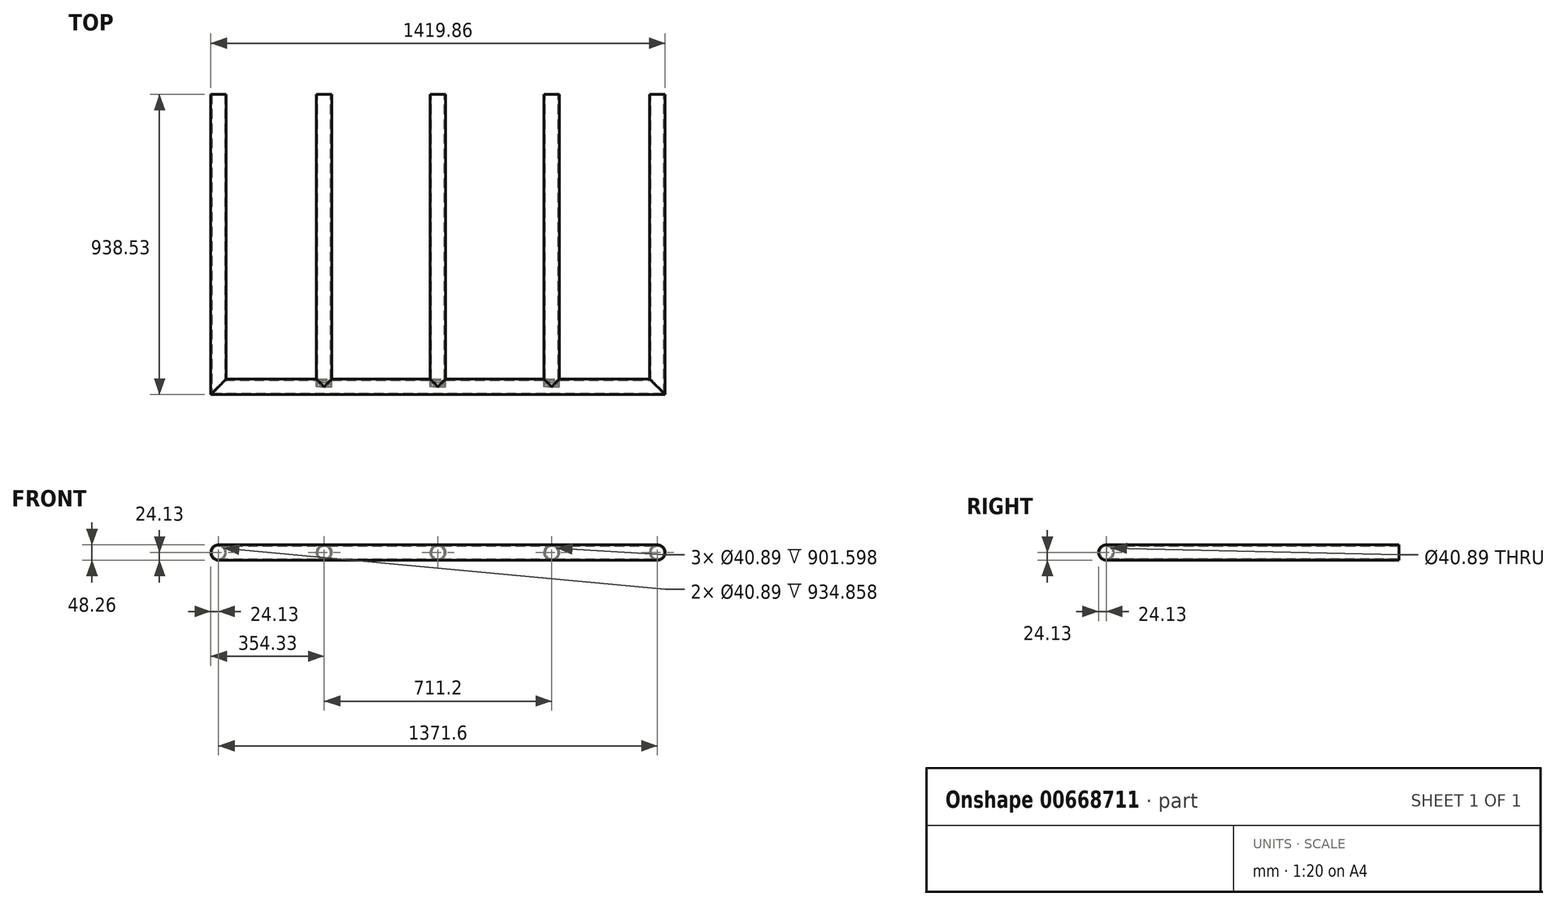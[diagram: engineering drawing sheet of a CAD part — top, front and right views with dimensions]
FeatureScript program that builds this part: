
annotation { "Feature Type Name" : "Feature", "Feature Type Description" : "" }
export const myFeature = defineFeature(function(context is Context, id is Id, definition is map)
    precondition{}
    {
        {
            var Q0;
            Q0=qCreatedBy(makeId("Front.planeOp"),FACE);
            var sketch = newSketch(context, id + "F0", { "sketchPlane" : qUnion([Q0])});
            skCircle(sketch, "E0", {"center": v(-685.8, 0) * mm, "radius": 24.13 * mm});
            skCircle(sketch, "E1", {"center": v(685.8, 0) * mm, "radius": 24.13 * mm});
            skCircle(sketch, "E2", {"center": v(685.8, 0) * mm, "radius": 20.45 * mm});
            skCircle(sketch, "E3", {"center": v(-685.8, 0) * mm, "radius": 20.45 * mm});
            skSolve(sketch);
        }
        {
            var Q0;
            Q0=qCreatedBy(makeId("Top.planeOp"),FACE);
            var sketch = newSketch(context, id + "F1", { "sketchPlane" : qUnion([Q0])});
            skLineSegment(sketch, "E4", {"start": v(-685.8, 0) * mm, "end": v(-685.8, -1016) * mm});
            skLineSegment(sketch, "E5", {"start": v(685.8, 0) * mm, "end": v(685.8, -1016) * mm});
            skLineSegment(sketch, "E6", {"start": v(-685.8, -1016) * mm, "end": v(685.8, -1016) * mm});
            skPoint(sketch, "E7.visualSharp", {"position": v(-685.8, -1016) * mm});
            skLineSegment(sketch, "E7.filletArc", {"start": v(-685.8, -1016) * mm, "end": v(-685.8, -1016) * mm});
            skPoint(sketch, "E8.visualSharp", {"position": v(685.8, -1016) * mm});
            skLineSegment(sketch, "E8.filletArc", {"start": v(685.8, -1016) * mm, "end": v(685.8, -1016) * mm});
            skLineSegment(sketch, "E9", {"start": v(-355.6, -1016) * mm, "end": v(-355.6, 0) * mm});
            skLineSegment(sketch, "E10", {"start": v(355.6, -1016) * mm, "end": v(355.6, 0) * mm});
            skLineSegment(sketch, "E11", {"start": v(0, -1016) * mm, "end": v(0, 0) * mm});
            skPoint(sketch, "E12", {"position": v(-685.8, -914.4) * mm});
            skPoint(sketch, "E13", {"position": v(685.8, -914.4) * mm});
            skPoint(sketch, "E14", {"position": v(-685.8, 0) * mm});
            skPoint(sketch, "E15", {"position": v(685.8, 0) * mm});
            skPoint(sketch, "E16", {"position": v(-355.6, -1016) * mm});
            skPoint(sketch, "E17", {"position": v(355.6, -1016) * mm});
            skSolve(sketch);
        }
        {
            var Q0;
            Q0=qCreatedBy(makeId("Front.planeOp"),FACE);
            var sketch = newSketch(context, id + "F2", { "sketchPlane" : qUnion([Q0])});
            skCircle(sketch, "E18", {"center": v(-355.6, 0) * mm, "radius": 24.13 * mm});
            skCircle(sketch, "E19", {"center": v(0, 0) * mm, "radius": 24.13 * mm});
            skCircle(sketch, "E20", {"center": v(355.6, 0) * mm, "radius": 24.13 * mm});
            skCircle(sketch, "E21", {"center": v(355.6, 0) * mm, "radius": 20.45 * mm});
            skCircle(sketch, "E22", {"center": v(0, 0) * mm, "radius": 20.45 * mm});
            skCircle(sketch, "E23", {"center": v(-355.6, 0) * mm, "radius": 20.45 * mm});
            skSolve(sketch);
        }
        {
            var Q0;
            Q0=makeQuery(id+"F0.imprint","IMPRINT",FACE,{"disambiguationData":[TD([[makeQuery(id+"F0.imprint","IMPRINT",EDGE,{"derivedFrom":sQuery(id+"F0.wireOp",EDGE,"E0")}),1.0]])]});
            var Q1;
            Q1=sQuery(id+"F1.wireOp",EDGE,"E4");
            var Q2;
            Q2=sQuery(id+"F1.wireOp",EDGE,"E7.filletArc");
            var Q3;
            Q3=sQuery(id+"F1.wireOp",EDGE,"E6");
            var Q4;
            Q4=sQuery(id+"F1.wireOp",EDGE,"E8.filletArc");
            var Q5;
            Q5=sQuery(id+"F1.wireOp",EDGE,"E5");
            sweep(context, id + "F3", {"profiles" : qUnion([Q0]), "path" : qUnion([Q1, Q2, Q3, Q4, Q5])});
        }
        {
            var Q0;
            Q0=makeQuery(id+"F2.imprint","IMPRINT",FACE,{"disambiguationData":[TD([[makeQuery(id+"F2.imprint","IMPRINT",EDGE,{"derivedFrom":sQuery(id+"F2.wireOp",EDGE,"E18")}),1.0]])]});
            var Q1;
            Q1=makeQuery(id+"F2.imprint","IMPRINT",FACE,{"disambiguationData":[TD([[makeQuery(id+"F2.imprint","IMPRINT",EDGE,{"derivedFrom":sQuery(id+"F2.wireOp",EDGE,"E19")}),1.0]])]});
            var Q2;
            Q2=makeQuery(id+"F2.imprint","IMPRINT",FACE,{"disambiguationData":[TD([[makeQuery(id+"F2.imprint","IMPRINT",EDGE,{"derivedFrom":sQuery(id+"F2.wireOp",EDGE,"E20")}),1.0]])]});
            extrude(context, id + "F4", {"entities" : qUnion([Q0, Q1, Q2]), "operationType" : NewBodyOperationType.ADD, "depth" : 1016 * mm});
        }
        {
            var Q0;
            Q0=qCreatedBy(makeId("Right.planeOp"),FACE);
            var sketch = newSketch(context, id + "F5", { "sketchPlane" : qUnion([Q0])});
            skLineSegment(sketch, "E24.bottom", {"start": v(-101.6, 47.84) * mm, "end": v(101.6, 47.84) * mm});
            skLineSegment(sketch, "E24.top", {"start": v(-101.6, -47.84) * mm, "end": v(101.6, -47.84) * mm});
            skLineSegment(sketch, "E24.left", {"start": v(-101.6, 47.84) * mm, "end": v(-101.6, -47.84) * mm});
            skLineSegment(sketch, "E24.right", {"start": v(101.6, 47.84) * mm, "end": v(101.6, -47.84) * mm});
            skPoint(sketch, "E24.middle", {"position": v(0, 0) * mm});
            skSolve(sketch);
        }
        {
            var Q0;
            Q0=qSketchRegion(id+"F5",true);
            extrude(context, id + "F6", {"entities" : qUnion([Q0]), "operationType" : NewBodyOperationType.REMOVE, "endBound" : BoundingType.THROUGH_ALL, "oppositeDirection" : true, "depth" : 25.4 * mm, "hasSecondDirection" : true, "secondDirectionBound" : SecondDirectionBoundingType.THROUGH_ALL, "secondDirectionOppositeDirection" : false, "secondDirectionDepth" : 25.4 * mm});
        }
    });
